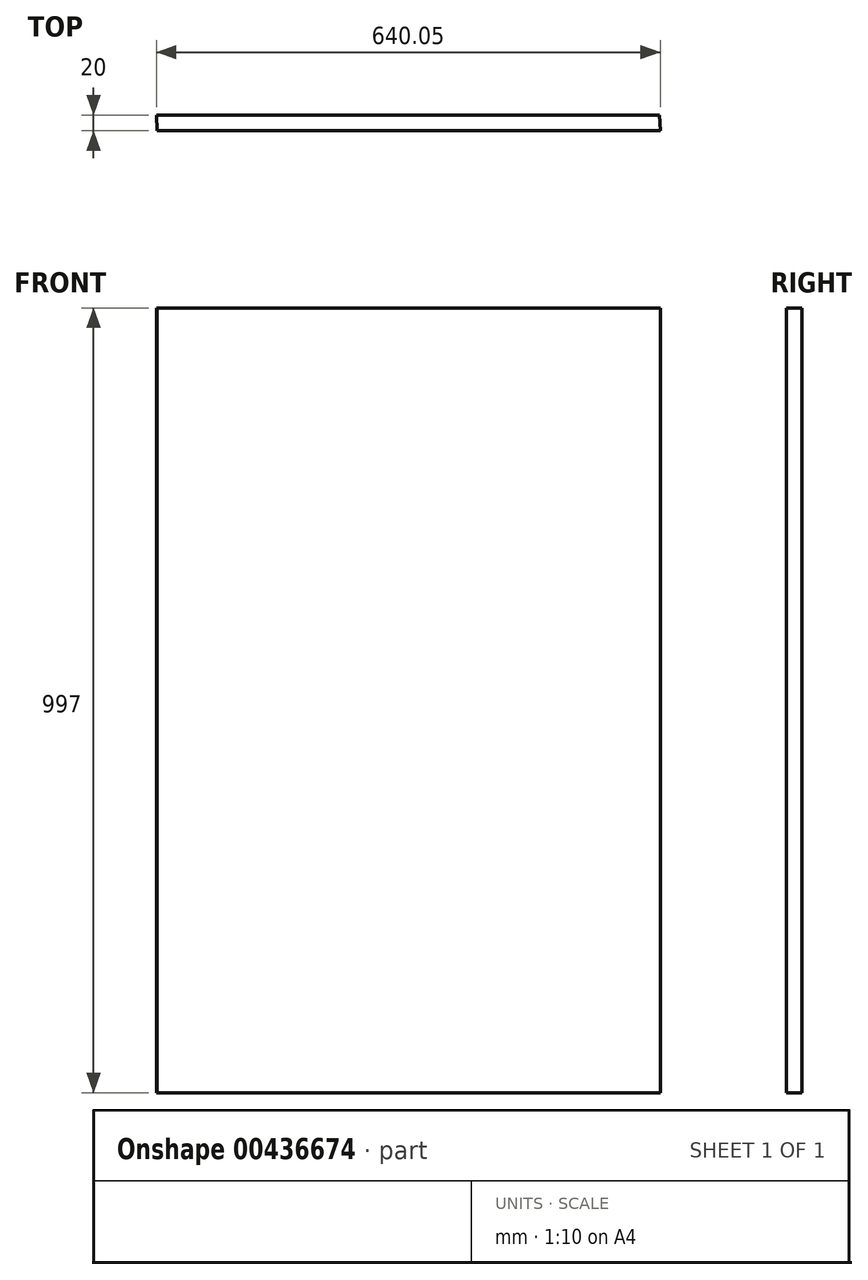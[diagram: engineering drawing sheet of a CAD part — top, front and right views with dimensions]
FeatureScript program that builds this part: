
annotation { "Feature Type Name" : "Feature", "Feature Type Description" : "" }
export const myFeature = defineFeature(function(context is Context, id is Id, definition is map)
    precondition{}
    {
        {
            var Q0;
            Q0=qCreatedBy(makeId("Top.planeOp"),FACE);
            var sketch = newSketch(context, id + "F0", { "sketchPlane" : qUnion([Q0])});
            skLineSegment(sketch, "E0.bottom", {"start": v(388.18, 85.64) * mm, "end": v(-250.82, 85.64) * mm});
            skLineSegment(sketch, "E0.top", {"start": v(387.13, 105.64) * mm, "end": v(-251.87, 105.64) * mm});
            skPoint(sketch, "E0.middle", {"position": v(0, 0) * mm});
            skLineSegment(sketch, "E1", {"start": v(-251.87, 105.64) * mm, "end": v(-250.82, 85.64) * mm});
            skLineSegment(sketch, "E2", {"start": v(387.13, 105.64) * mm, "end": v(388.18, 85.64) * mm});
            skSolve(sketch);
        }
        {
            var Q0;
            Q0=qSketchRegion(id+"F0",true);
            extrude(context, id + "F1", {"entities" : qUnion([Q0]), "depth" : 997 * mm});
        }
    });
